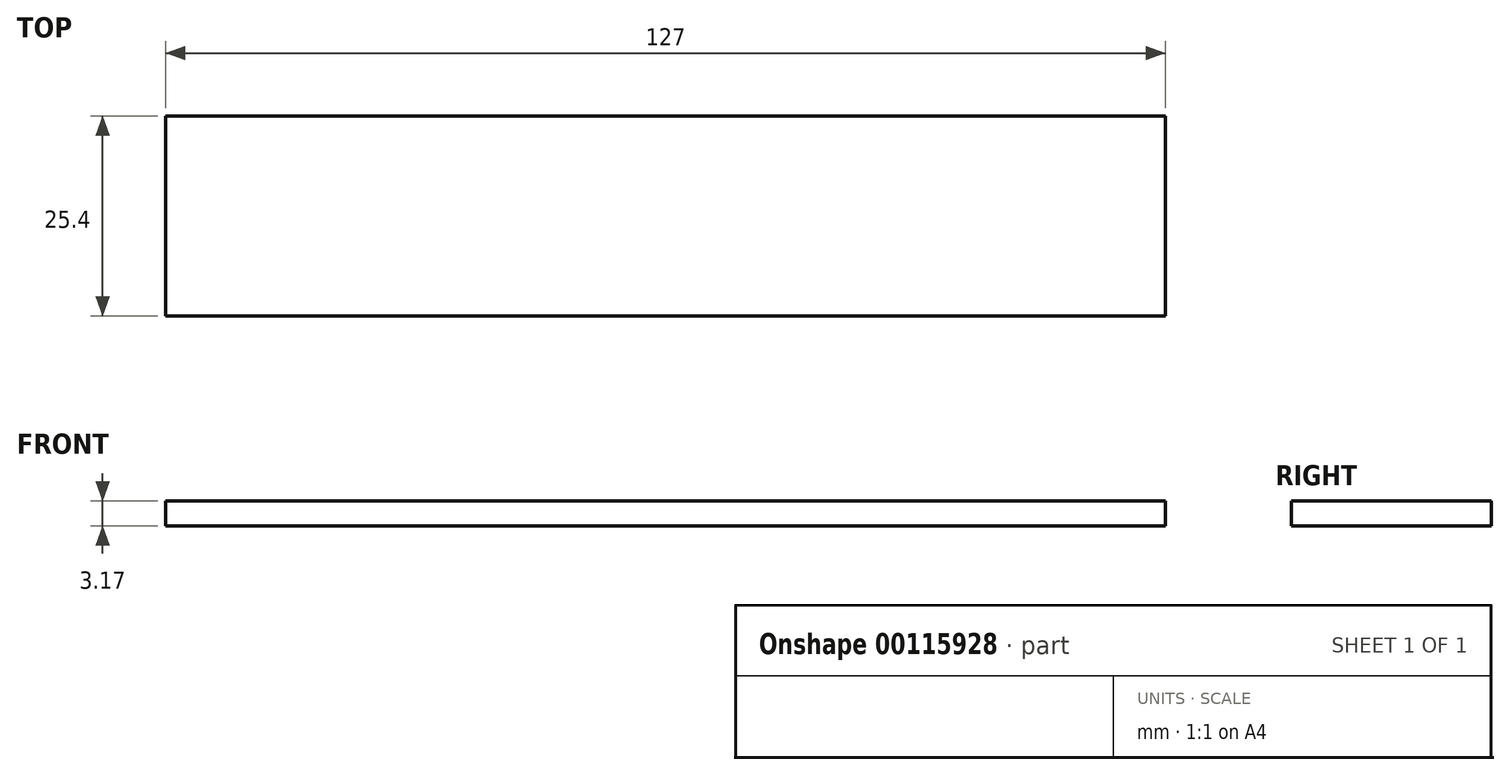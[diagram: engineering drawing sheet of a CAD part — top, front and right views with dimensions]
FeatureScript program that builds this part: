
annotation { "Feature Type Name" : "Feature", "Feature Type Description" : "" }
export const myFeature = defineFeature(function(context is Context, id is Id, definition is map)
    precondition{}
    {
        {
            var Q0;
            Q0=qCreatedBy(makeId("Top.planeOp"),FACE);
            var sketch = newSketch(context, id + "F0", { "sketchPlane" : qUnion([Q0])});
            skLineSegment(sketch, "E0.bottom", {"start": v(-12.71, 15.17) * mm, "end": v(114.29, 15.17) * mm});
            skLineSegment(sketch, "E0.top", {"start": v(-12.71, -10.23) * mm, "end": v(114.29, -10.23) * mm});
            skLineSegment(sketch, "E0.left", {"start": v(-12.71, 15.17) * mm, "end": v(-12.71, -10.23) * mm});
            skLineSegment(sketch, "E0.right", {"start": v(114.29, 15.17) * mm, "end": v(114.29, -10.23) * mm});
            skSolve(sketch);
        }
        {
            var Q0;
            Q0=makeQuery(id+"F0.imprint","IMPRINT",FACE,{"disambiguationData":[TD([[makeQuery(id+"F0.imprint","IMPRINT",EDGE,{"derivedFrom":sQuery(id+"F0.wireOp",EDGE,"E0.bottom")}),-1.0]])]});
            extrude(context, id + "F1", {"entities" : qUnion([Q0]), "depth" : 3.17 * mm});
        }
    });
